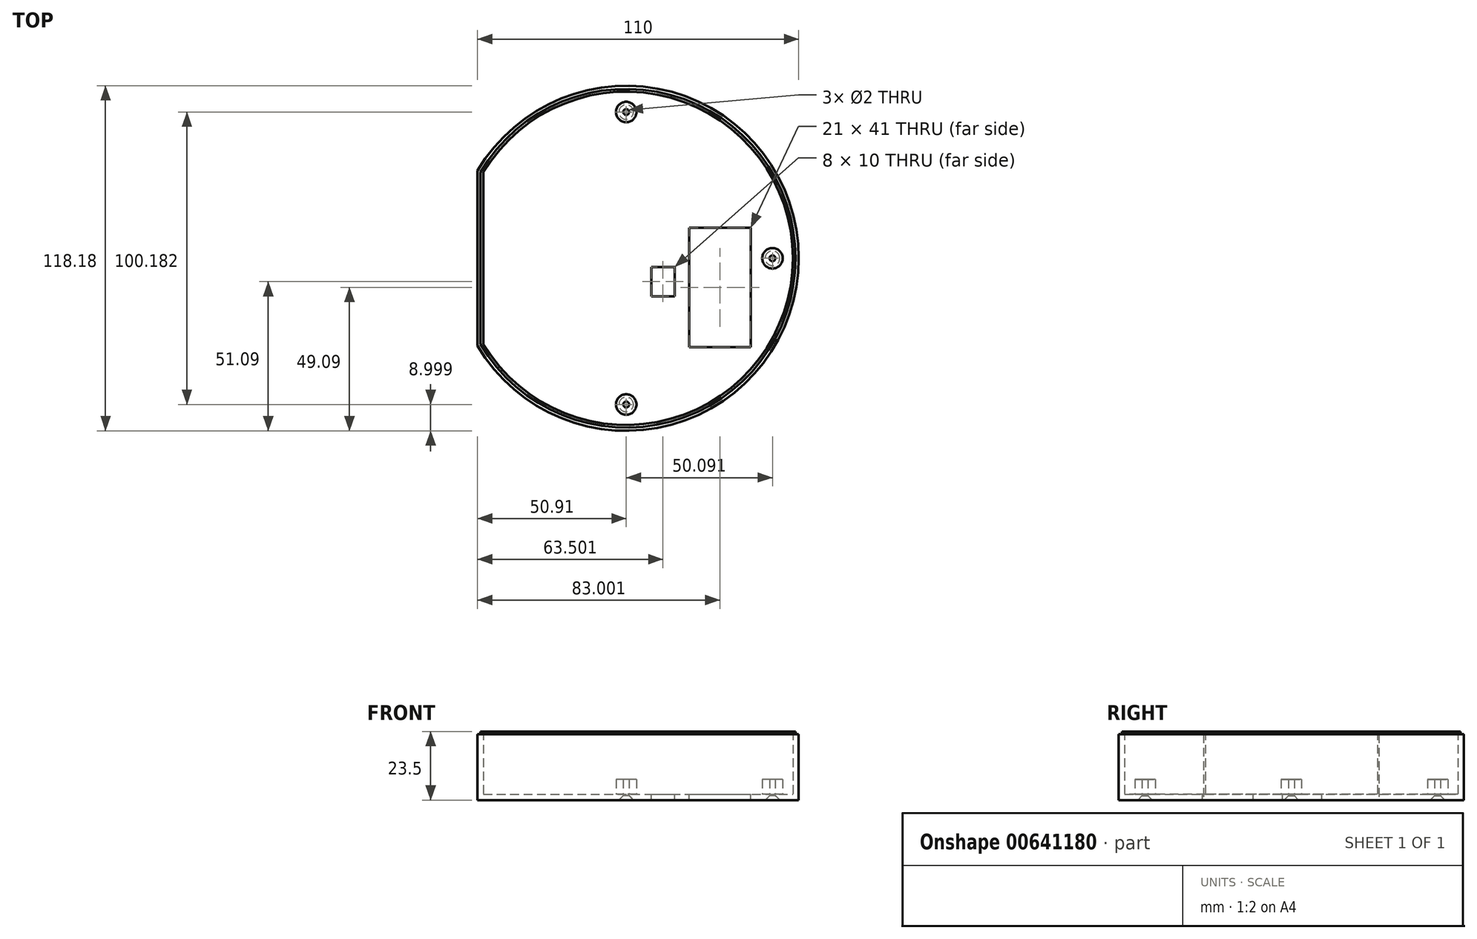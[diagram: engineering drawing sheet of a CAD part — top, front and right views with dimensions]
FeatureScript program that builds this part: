
annotation { "Feature Type Name" : "Feature", "Feature Type Description" : "" }
export const myFeature = defineFeature(function(context is Context, id is Id, definition is map)
    precondition{}
    {
        {
            var Q0;
            Q0=qCreatedBy(makeId("Top.planeOp"),FACE);
            var sketch = newSketch(context, id + "F0", { "sketchPlane" : qUnion([Q0])});
            skArc(sketch, "E0", {"start": v(-50.9, -30) * mm, "mid": v(59.1, 0) * mm, "end": v(-50.9, 30) * mm});
            skLineSegment(sketch, "E1", {"start": v(-50.9, 30) * mm, "end": v(-50.9, -30) * mm});
            skSolve(sketch);
        }
        {
            var Q0;
            Q0=makeQuery(id+"F0.imprint","IMPRINT",FACE,{"disambiguationData":[TD([[makeQuery(id+"F0.imprint","IMPRINT",EDGE,{"derivedFrom":sQuery(id+"F0.wireOp",EDGE,"E0")}),1.0]])]});
            extrude(context, id + "F1", {"entities" : qUnion([Q0]), "depth" : 2 * mm, "offsetDistance" : 25 * mm});
        }
        {
            var Q0;
            Q0=makeQuery(id+"F1.opExtrude","CAP_FACE",FACE,{"disambiguationData":[OSD([sQuery(id+"F0.wireOp",EDGE,"E0"),sQuery(id+"F0.wireOp",EDGE,"E1")])],"isStart":false});
            var sketch = newSketch(context, id + "F2", { "sketchPlane" : qUnion([Q0])});
            skArc(sketch, "E2", {"start": v(-48.9, -29.45) * mm, "mid": v(57.1, 0) * mm, "end": v(-48.9, 29.45) * mm});
            skLineSegment(sketch, "E3", {"start": v(-48.9, 29.45) * mm, "end": v(-48.9, -29.45) * mm});
            skLineSegment(sketch, "E4.bottom", {"start": v(-48.9, -24.85) * mm, "end": v(19.6, -24.85) * mm, "construction": true});
            skLineSegment(sketch, "E4.top", {"start": v(-48.9, 28.45) * mm, "end": v(19.6, 28.45) * mm, "construction": true});
            skLineSegment(sketch, "E4.left", {"start": v(-48.9, -24.85) * mm, "end": v(-48.9, 28.45) * mm, "construction": true});
            skLineSegment(sketch, "E4.right", {"start": v(19.6, -24.85) * mm, "end": v(19.6, 28.45) * mm, "construction": true});
            skLineSegment(sketch, "E5", {"start": v(-50.9, 19.35) * mm, "end": v(-48.9, 19.35) * mm});
            skLineSegment(sketch, "E6", {"start": v(-50.9, 6.35) * mm, "end": v(-48.9, 6.35) * mm});
            skLineSegment(sketch, "E7", {"start": v(-50.9, -12.05) * mm, "end": v(-48.9, -12.05) * mm});
            skLineSegment(sketch, "E8", {"start": v(-50.9, -22.05) * mm, "end": v(-48.9, -22.05) * mm});
            skCircle(sketch, "E9", {"center": v(-34.9, -22.35) * mm, "radius": 2 * mm});
            skCircle(sketch, "E10", {"center": v(-33.6, 25.95) * mm, "radius": 2 * mm});
            skCircle(sketch, "E11", {"center": v(17.2, 10.75) * mm, "radius": 2 * mm});
            skLineSegment(sketch, "E12", {"start": v(17.2, 10.75) * mm, "end": v(17.2, -19.32) * mm, "construction": true});
            skCircle(sketch, "E13", {"center": v(17.2, -17.15) * mm, "radius": 2 * mm});
            skCircle(sketch, "E14", {"center": v(-33.6, 25.95) * mm, "radius": 1.25 * mm});
            skCircle(sketch, "E15", {"center": v(-34.9, -22.35) * mm, "radius": 1.25 * mm});
            skCircle(sketch, "E16", {"center": v(17.2, 10.75) * mm, "radius": 1.25 * mm});
            skCircle(sketch, "E17", {"center": v(17.2, -17.15) * mm, "radius": 1.25 * mm});
            skSolve(sketch);
        }
        {
            var Q0;
            {var subQ4=sQuery(id+"F2.wireOp",EDGE,"E2");Q0=makeQuery(id+"F2.imprint","IMPRINT",FACE,{"disambiguationData":[TD([[makeQuery(id+"F2.imprint","IMPRINT",EDGE,{"derivedFrom":subQ4}),1.0]])]});}
            var sketch = newSketch(context, id + "F3", { "sketchPlane" : qUnion([Q0])});
            skCircle(sketch, "E18", {"center": v(50.1, 0) * mm, "radius": 3.5 * mm});
            skCircle(sketch, "E19", {"center": v(0, 50.1) * mm, "radius": 3.5 * mm});
            skCircle(sketch, "E20", {"center": v(0, -50.1) * mm, "radius": 3.5 * mm});
            skCircle(sketch, "E21", {"center": v(0, -50.1) * mm, "radius": 1 * mm});
            skCircle(sketch, "E22", {"center": v(0, 50.1) * mm, "radius": 1 * mm});
            skCircle(sketch, "E23", {"center": v(50.1, 0) * mm, "radius": 1 * mm});
            skSolve(sketch);
        }
        {
            var Q0;
            {var subQ4=sQuery(id+"F2.wireOp",EDGE,"E2");Q0=makeQuery(id+"F2.imprint","IMPRINT",FACE,{"disambiguationData":[TD([[makeQuery(id+"F2.imprint","IMPRINT",EDGE,{"derivedFrom":subQ4}),1.0]])]});}
            var sketch = newSketch(context, id + "F4", { "sketchPlane" : qUnion([Q0])});
            skLineSegment(sketch, "E24", {"start": v(21.6, 10.5) * mm, "end": v(42.6, 10.5) * mm});
            skLineSegment(sketch, "E25", {"start": v(42.6, 10.5) * mm, "end": v(42.6, -30.5) * mm});
            skLineSegment(sketch, "E26", {"start": v(42.6, -30.5) * mm, "end": v(21.6, -30.5) * mm});
            skLineSegment(sketch, "E27", {"start": v(21.6, 10.5) * mm, "end": v(21.6, -30.5) * mm});
            skLineSegment(sketch, "E28.bottom", {"start": v(8.6, -3) * mm, "end": v(16.6, -3) * mm});
            skLineSegment(sketch, "E28.top", {"start": v(8.6, -13) * mm, "end": v(16.6, -13) * mm});
            skLineSegment(sketch, "E28.left", {"start": v(8.6, -3) * mm, "end": v(8.6, -13) * mm});
            skLineSegment(sketch, "E28.right", {"start": v(16.6, -3) * mm, "end": v(16.6, -13) * mm});
            skSolve(sketch);
        }
        {
            var Q0;
            Q0=makeQuery(id+"F3.imprint","IMPRINT",FACE,{"disambiguationData":[TD([[makeQuery(id+"F3.imprint","IMPRINT",EDGE,{"derivedFrom":sQuery(id+"F3.wireOp",EDGE,"E20")}),1.0]])]});
            var Q1;
            Q1=makeQuery(id+"F3.imprint","IMPRINT",FACE,{"disambiguationData":[TD([[makeQuery(id+"F3.imprint","IMPRINT",EDGE,{"derivedFrom":sQuery(id+"F3.wireOp",EDGE,"E19")}),1.0]])]});
            var Q2;
            Q2=makeQuery(id+"F3.imprint","IMPRINT",FACE,{"disambiguationData":[TD([[makeQuery(id+"F3.imprint","IMPRINT",EDGE,{"derivedFrom":sQuery(id+"F3.wireOp",EDGE,"E18")}),1.0]])]});
            extrude(context, id + "F5", {"entities" : qUnion([Q0, Q1, Q2]), "operationType" : NewBodyOperationType.ADD, "depth" : 5 * mm, "offsetDistance" : 25 * mm});
        }
        {
            var Q0;
            {var subQ2=sQuery(id+"F2.wireOp",EDGE,"E2");Q0=makeQuery(id+"F2.imprint","IMPRINT",FACE,{"disambiguationData":[TD([[makeQuery(id+"F2.imprint","IMPRINT",EDGE,{"derivedFrom":subQ2}),-1.0]])]});}
            var Q1;
            {var subQ0=sQuery(id+"F2.wireOp",EDGE,"E5");Q1=makeQuery(id+"F2.imprint","IMPRINT",FACE,{"disambiguationData":[TD([[makeQuery(id+"F2.imprint","IMPRINT",EDGE,{"derivedFrom":subQ0}),-1.0]])]});}
            var Q2;
            {var subQ0=sQuery(id+"F2.wireOp",EDGE,"E6");Q2=makeQuery(id+"F2.imprint","IMPRINT",FACE,{"disambiguationData":[TD([[makeQuery(id+"F2.imprint","IMPRINT",EDGE,{"derivedFrom":subQ0}),-1.0]])]});}
            var Q3;
            {var subQ0=sQuery(id+"F2.wireOp",EDGE,"E7");Q3=makeQuery(id+"F2.imprint","IMPRINT",FACE,{"disambiguationData":[TD([[makeQuery(id+"F2.imprint","IMPRINT",EDGE,{"derivedFrom":subQ0}),-1.0]])]});}
            extrude(context, id + "F6", {"entities" : qUnion([Q0, Q1, Q2, Q3]), "operationType" : NewBodyOperationType.ADD, "depth" : 20.5 * mm, "offsetDistance" : 25 * mm});
        }
        {
            var Q0;
            Q0=makeQuery(id+"F6.opExtrude","CAP_FACE",FACE,{"disambiguationData":[OSD([sQuery(id+"F0.wireOp",EDGE,"E0"),sQuery(id+"F0.wireOp",EDGE,"E1"),sQuery(id+"F2.wireOp",EDGE,"E2"),sQuery(id+"F2.wireOp",EDGE,"E3")])],"isStart":false});
            var sketch = newSketch(context, id + "F7", { "sketchPlane" : qUnion([Q0])});
            skArc(sketch, "E29.0", {"start": v(-48.9, -29.45) * mm, "mid": v(57.1, 0) * mm, "end": v(-48.9, 29.45) * mm, "construction": true});
            skLineSegment(sketch, "E29.1", {"start": v(-48.9, 29.45) * mm, "end": v(-48.9, -29.45) * mm, "construction": true});
            skArc(sketch, "E30", {"start": v(-48.9, -29.45) * mm, "mid": v(57.1, 0) * mm, "end": v(-48.9, 29.45) * mm});
            skArc(sketch, "E31", {"start": v(-49.96, -29.45) * mm, "mid": v(58, 0) * mm, "end": v(-49.96, 29.45) * mm});
            skLineSegment(sketch, "E32", {"start": v(-49.96, -29.45) * mm, "end": v(-49.96, 29.45) * mm});
            skLineSegment(sketch, "E33", {"start": v(-48.9, 29.45) * mm, "end": v(-48.9, -29.45) * mm});
            skSolve(sketch);
        }
        {
            var Q0;
            Q0=makeQuery(id+"F7.imprint","IMPRINT",FACE,{"disambiguationData":[TD([[makeQuery(id+"F7.imprint","IMPRINT",EDGE,{"derivedFrom":sQuery(id+"F7.wireOp",EDGE,"E30")}),-1.0]])]});
            extrude(context, id + "F8", {"entities" : qUnion([Q0]), "operationType" : NewBodyOperationType.ADD, "depth" : 1 * mm, "offsetDistance" : 25 * mm});
        }
        {
            var Q0;
            Q0=makeQuery(id+"F4.imprint","IMPRINT",FACE,{"disambiguationData":[TD([[makeQuery(id+"F4.imprint","IMPRINT",EDGE,{"derivedFrom":sQuery(id+"F4.wireOp",EDGE,"E24")}),-1.0]])]});
            extrude(context, id + "F9", {"entities" : qUnion([Q0]), "operationType" : NewBodyOperationType.REMOVE, "oppositeDirection" : true, "depth" : 25 * mm, "offsetDistance" : 25 * mm});
        }
        {
            var Q0;
            Q0=makeQuery(id+"F3.imprint","IMPRINT",FACE,{"disambiguationData":[TD([[makeQuery(id+"F3.imprint","IMPRINT",EDGE,{"derivedFrom":sQuery(id+"F3.wireOp",EDGE,"E22")}),1.0]])]});
            var Q1;
            Q1=makeQuery(id+"F3.imprint","IMPRINT",FACE,{"disambiguationData":[TD([[makeQuery(id+"F3.imprint","IMPRINT",EDGE,{"derivedFrom":sQuery(id+"F3.wireOp",EDGE,"E23")}),1.0]])]});
            var Q2;
            Q2=makeQuery(id+"F3.imprint","IMPRINT",FACE,{"disambiguationData":[TD([[makeQuery(id+"F3.imprint","IMPRINT",EDGE,{"derivedFrom":sQuery(id+"F3.wireOp",EDGE,"E21")}),1.0]])]});
            extrude(context, id + "F10", {"entities" : qUnion([Q0, Q1, Q2]), "operationType" : NewBodyOperationType.REMOVE, "oppositeDirection" : true, "depth" : 25 * mm, "offsetDistance" : 25 * mm});
        }
        {
            var Q0;
            Q0=makeQuery(id+"F10.boolean.opBoolean","INTERSECT",EDGE,{"derivedFrom":[makeQuery(id+"F1.opExtrude","CAP_FACE",FACE,{"disambiguationData":[OSD([sQuery(id+"F0.wireOp",EDGE,"E0"),sQuery(id+"F0.wireOp",EDGE,"E1")])],"isStart":true}),makeQuery(id+"F10.opExtrude","SWEPT_FACE",FACE,{"disambiguationData":[OSD([sQuery(id+"F3.wireOp",EDGE,"E21")])]})]});
            var Q1;
            Q1=makeQuery(id+"F10.boolean.opBoolean","INTERSECT",EDGE,{"derivedFrom":[makeQuery(id+"F1.opExtrude","CAP_FACE",FACE,{"disambiguationData":[OSD([sQuery(id+"F0.wireOp",EDGE,"E0"),sQuery(id+"F0.wireOp",EDGE,"E1")])],"isStart":true}),makeQuery(id+"F10.opExtrude","SWEPT_FACE",FACE,{"disambiguationData":[OSD([sQuery(id+"F3.wireOp",EDGE,"E23")])]})]});
            var Q2;
            Q2=makeQuery(id+"F10.boolean.opBoolean","INTERSECT",EDGE,{"derivedFrom":[makeQuery(id+"F1.opExtrude","CAP_FACE",FACE,{"disambiguationData":[OSD([sQuery(id+"F0.wireOp",EDGE,"E0"),sQuery(id+"F0.wireOp",EDGE,"E1")])],"isStart":true}),makeQuery(id+"F10.opExtrude","SWEPT_FACE",FACE,{"disambiguationData":[OSD([sQuery(id+"F3.wireOp",EDGE,"E22")])]})]});
            chamfer(context, id + "F11", {"entities" : qUnion([Q0, Q1, Q2]), "chamferType" : ChamferType.OFFSET_ANGLE, "width" : 1.5 * mm, "oppositeDirection" : false, "angle" : 45 * degree, "tangentPropagation" : true});
        }
        {
            var Q0;
            Q0=makeQuery(id+"F4.imprint","IMPRINT",FACE,{"disambiguationData":[TD([[makeQuery(id+"F4.imprint","IMPRINT",EDGE,{"derivedFrom":sQuery(id+"F4.wireOp",EDGE,"E28.bottom")}),-1.0]])]});
            extrude(context, id + "F12", {"entities" : qUnion([Q0]), "operationType" : NewBodyOperationType.REMOVE, "oppositeDirection" : true, "depth" : 25 * mm, "offsetDistance" : 25 * mm});
        }
    });
